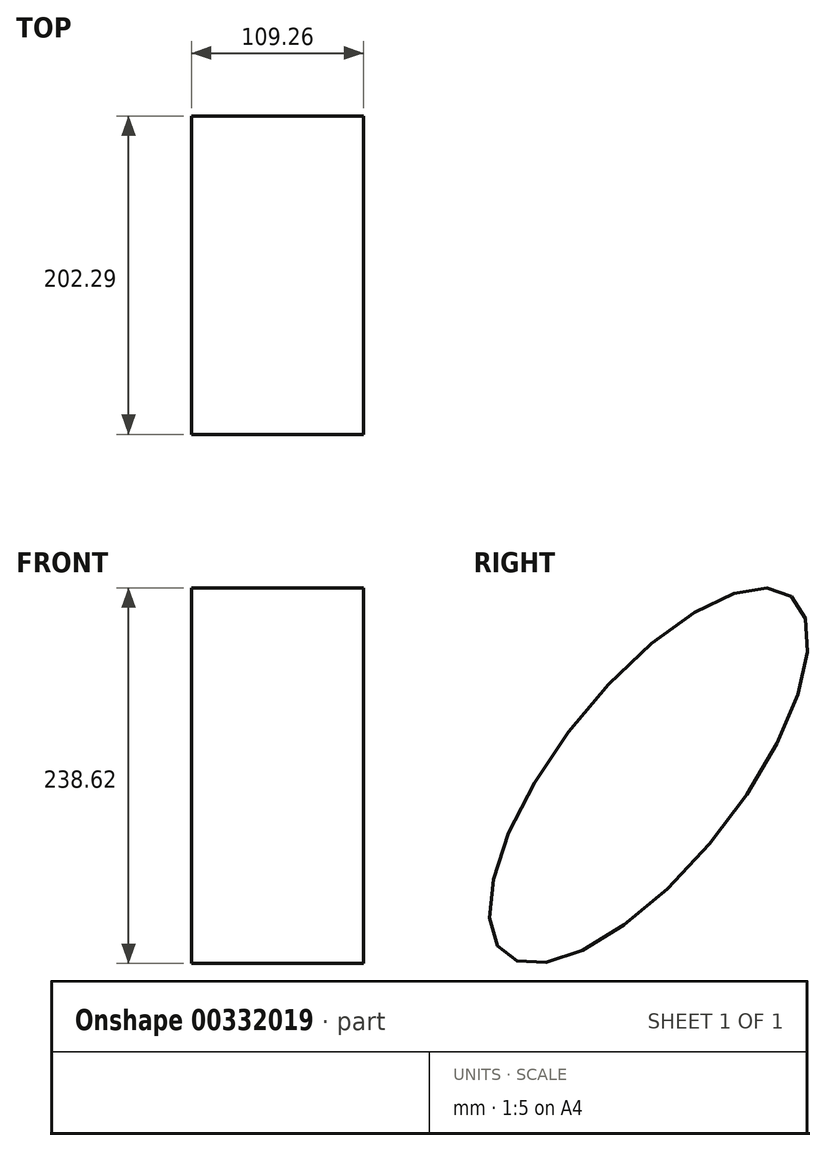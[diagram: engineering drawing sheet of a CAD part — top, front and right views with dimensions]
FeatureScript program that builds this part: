
annotation { "Feature Type Name" : "Feature", "Feature Type Description" : "" }
export const myFeature = defineFeature(function(context is Context, id is Id, definition is map)
    precondition{}
    {
        {
            var Q0;
            Q0=qCreatedBy(makeId("Right.planeOp"),FACE);
            var sketch = newSketch(context, id + "F0", { "sketchPlane" : qUnion([Q0])});
            skEllipse(sketch, "E0", {"center": v(-91.42, 0) * mm, "majorRadius": 145.52 * mm, "minorRadius": 57.34 * mm, "majorAxis": v(0.62, 0.78)});
            skSolve(sketch);
        }
        {
            var Q0;
            Q0=makeQuery(id+"F0.imprint","IMPRINT",FACE,{"disambiguationData":[TD([[makeQuery(id+"F0.imprint","IMPRINT",EDGE,{"derivedFrom":sQuery(id+"F0.wireOp",EDGE,"E0")}),1.0]])]});
            extrude(context, id + "F1", {"entities" : qUnion([Q0]), "depth" : 109.26 * mm});
        }
    });
